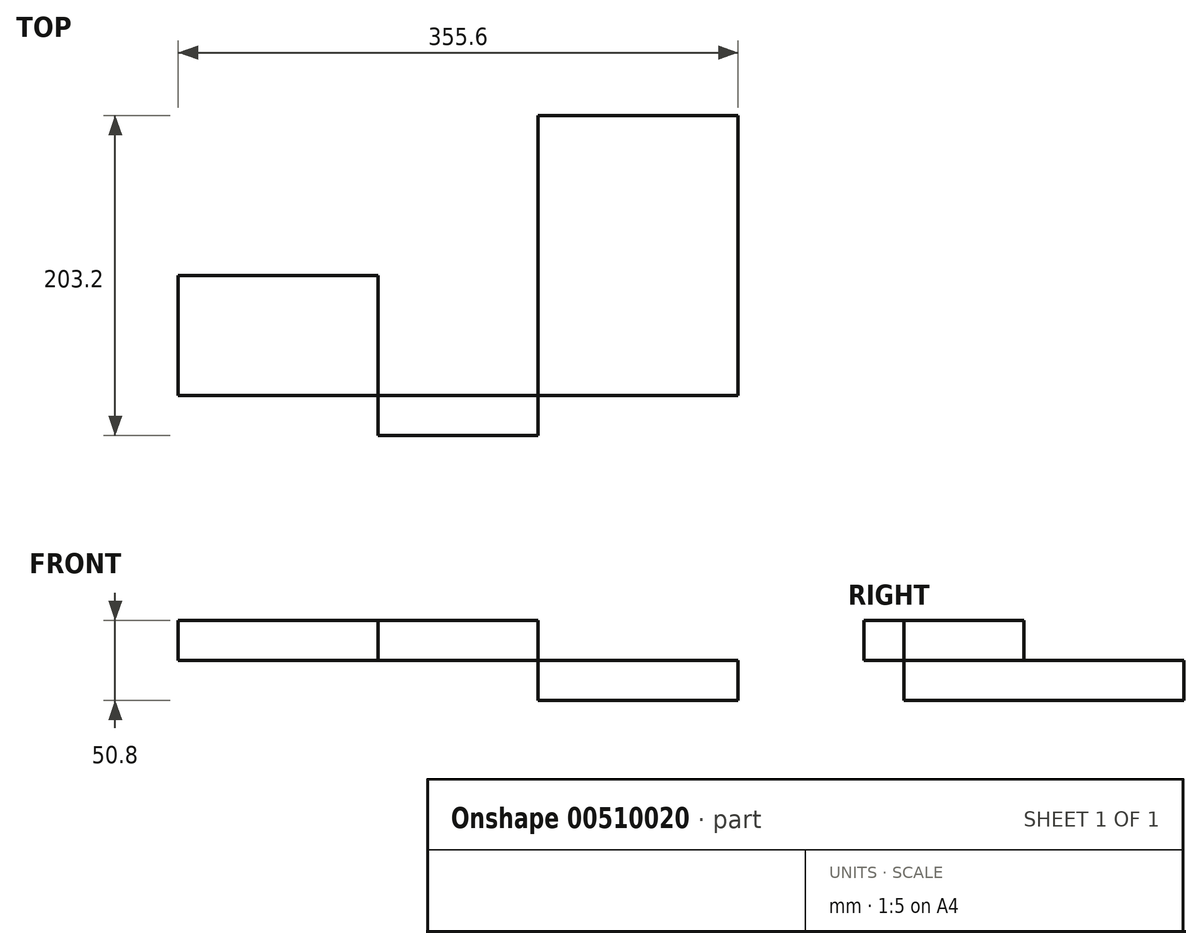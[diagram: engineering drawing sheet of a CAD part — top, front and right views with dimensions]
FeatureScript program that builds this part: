
annotation { "Feature Type Name" : "Feature", "Feature Type Description" : "" }
export const myFeature = defineFeature(function(context is Context, id is Id, definition is map)
    precondition{}
    {
        {
            var Q0;
            Q0=qCreatedBy(makeId("Top.planeOp"),FACE);
            var sketch = newSketch(context, id + "F0", { "sketchPlane" : qUnion([Q0])});
            skLineSegment(sketch, "E0.bottom", {"start": v(0, 0) * mm, "end": v(127, 0) * mm});
            skLineSegment(sketch, "E0.top", {"start": v(0, 76.2) * mm, "end": v(127, 76.2) * mm});
            skLineSegment(sketch, "E0.left", {"start": v(0, 0) * mm, "end": v(0, 76.2) * mm});
            skLineSegment(sketch, "E0.right", {"start": v(127, 0) * mm, "end": v(127, 76.2) * mm});
            skLineSegment(sketch, "E1.bottom", {"start": v(127, 0) * mm, "end": v(228.6, 0) * mm});
            skLineSegment(sketch, "E1.top", {"start": v(127, -25.4) * mm, "end": v(228.6, -25.4) * mm});
            skLineSegment(sketch, "E1.left", {"start": v(127, 0) * mm, "end": v(127, -25.4) * mm});
            skLineSegment(sketch, "E1.right", {"start": v(228.6, 0) * mm, "end": v(228.6, -25.4) * mm});
            skLineSegment(sketch, "E2.bottom", {"start": v(228.6, 0) * mm, "end": v(355.6, 0) * mm});
            skLineSegment(sketch, "E2.top", {"start": v(228.6, 177.8) * mm, "end": v(355.6, 177.8) * mm});
            skLineSegment(sketch, "E2.left", {"start": v(228.6, 0) * mm, "end": v(228.6, 177.8) * mm});
            skLineSegment(sketch, "E2.right", {"start": v(355.6, 0) * mm, "end": v(355.6, 177.8) * mm});
            skSolve(sketch);
        }
        {
            var Q0;
            Q0=makeQuery(id+"F0.imprint","IMPRINT",FACE,{"disambiguationData":[TD([[makeQuery(id+"F0.imprint","IMPRINT",EDGE,{"derivedFrom":sQuery(id+"F0.wireOp",EDGE,"E0.bottom")}),1.0]])]});
            var Q1;
            Q1=makeQuery(id+"F0.imprint","IMPRINT",FACE,{"disambiguationData":[TD([[makeQuery(id+"F0.imprint","IMPRINT",EDGE,{"derivedFrom":sQuery(id+"F0.wireOp",EDGE,"E1.bottom")}),-1.0]])]});
            extrude(context, id + "F1", {"entities" : qUnion([Q0, Q1]), "depth" : 25.4 * mm});
        }
        {
            var Q0;
            Q0=makeQuery(id+"F0.imprint","IMPRINT",FACE,{"disambiguationData":[TD([[makeQuery(id+"F0.imprint","IMPRINT",EDGE,{"derivedFrom":sQuery(id+"F0.wireOp",EDGE,"E2.bottom")}),1.0]])]});
            extrude(context, id + "F2", {"entities" : qUnion([Q0]), "oppositeDirection" : true, "depth" : 25.4 * mm});
        }
    });
